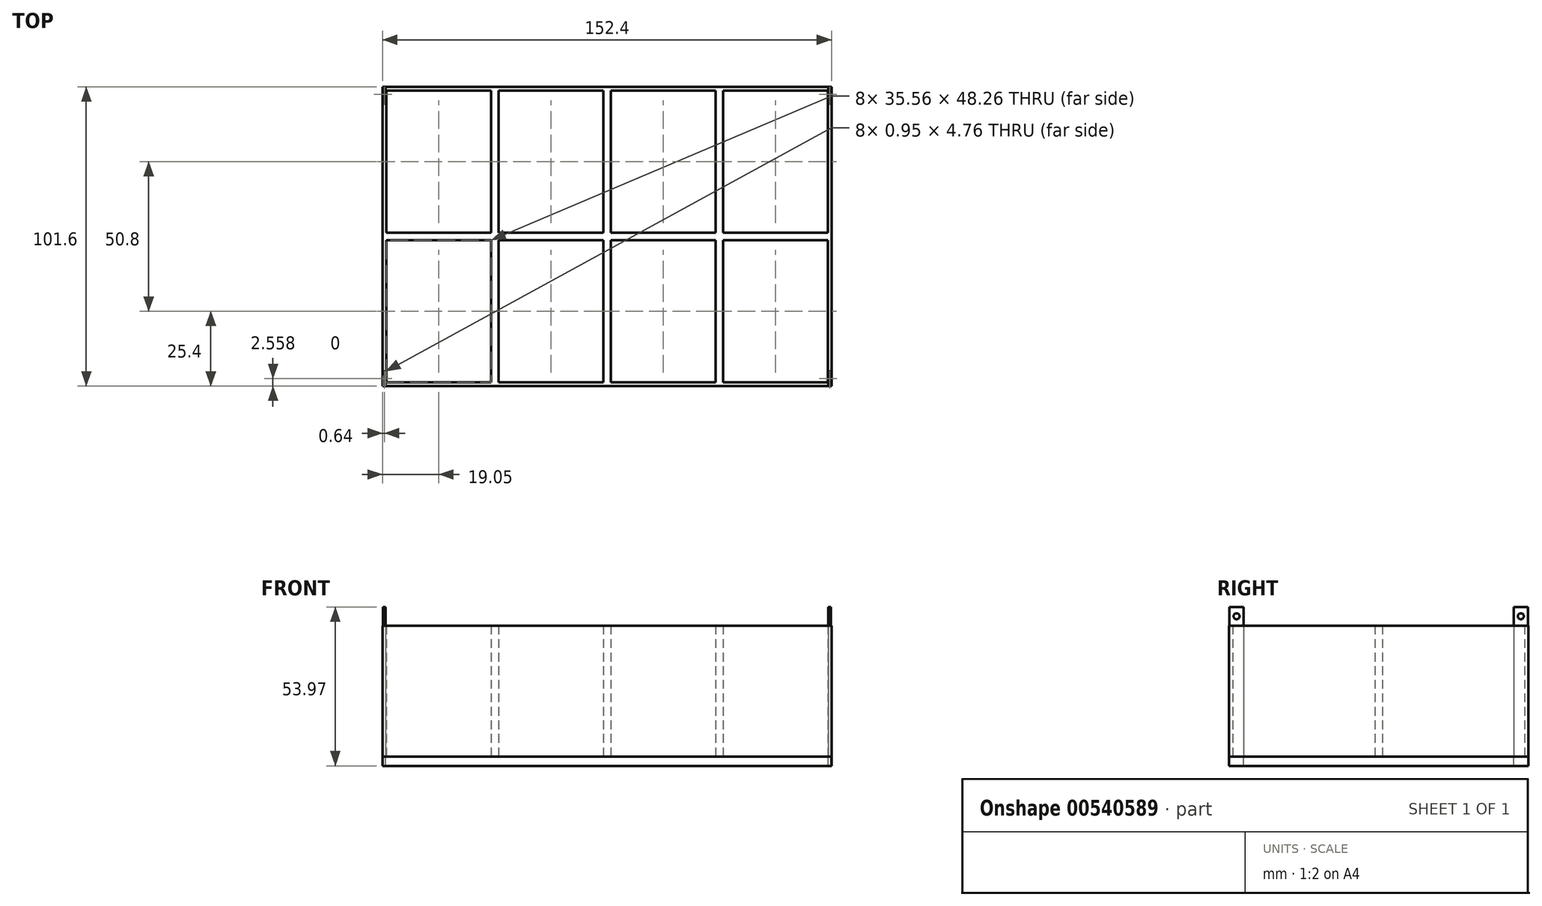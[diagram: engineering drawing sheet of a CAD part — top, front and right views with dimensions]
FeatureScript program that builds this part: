
annotation { "Feature Type Name" : "Feature", "Feature Type Description" : "" }
export const myFeature = defineFeature(function(context is Context, id is Id, definition is map)
    precondition{}
    {
        {
            var Q0;
            Q0=qCreatedBy(makeId("Top.planeOp"),FACE);
            var sketch = newSketch(context, id + "F0", { "sketchPlane" : qUnion([Q0])});
            skLineSegment(sketch, "E0.bottom", {"start": v(-76.2, 50.8) * mm, "end": v(76.2, 50.8) * mm});
            skLineSegment(sketch, "E0.top", {"start": v(-76.2, -50.8) * mm, "end": v(76.2, -50.8) * mm});
            skLineSegment(sketch, "E0.left", {"start": v(-76.2, 50.8) * mm, "end": v(-76.2, -50.8) * mm});
            skLineSegment(sketch, "E0.right", {"start": v(76.2, 50.8) * mm, "end": v(76.2, -50.8) * mm});
            skPoint(sketch, "E1", {"position": v(0, 0) * mm});
            skLineSegment(sketch, "E2.bottom", {"start": v(-74.93, 49.53) * mm, "end": v(-39.37, 49.53) * mm});
            skLineSegment(sketch, "E2.top", {"start": v(-74.93, 1.27) * mm, "end": v(-39.37, 1.27) * mm});
            skLineSegment(sketch, "E2.left", {"start": v(-74.93, 49.53) * mm, "end": v(-74.93, 1.27) * mm});
            skLineSegment(sketch, "E2.right", {"start": v(-39.37, 49.53) * mm, "end": v(-39.37, 1.27) * mm});
            skLineSegment(sketch, "E3.bottom", {"start": v(-36.83, 49.53) * mm, "end": v(-1.27, 49.53) * mm});
            skLineSegment(sketch, "E3.top", {"start": v(-36.83, 1.27) * mm, "end": v(-1.27, 1.27) * mm});
            skLineSegment(sketch, "E3.left", {"start": v(-36.83, 49.53) * mm, "end": v(-36.83, 1.27) * mm});
            skLineSegment(sketch, "E3.right", {"start": v(-1.27, 49.53) * mm, "end": v(-1.27, 1.27) * mm});
            skLineSegment(sketch, "E4.bottom", {"start": v(1.27, 49.53) * mm, "end": v(36.83, 49.53) * mm});
            skLineSegment(sketch, "E4.top", {"start": v(1.27, 1.27) * mm, "end": v(36.83, 1.27) * mm});
            skLineSegment(sketch, "E4.left", {"start": v(1.27, 49.53) * mm, "end": v(1.27, 1.27) * mm});
            skLineSegment(sketch, "E4.right", {"start": v(36.83, 49.53) * mm, "end": v(36.83, 1.27) * mm});
            skLineSegment(sketch, "E5.bottom", {"start": v(39.37, 49.53) * mm, "end": v(74.93, 49.53) * mm});
            skLineSegment(sketch, "E5.top", {"start": v(39.37, 1.27) * mm, "end": v(74.93, 1.27) * mm});
            skLineSegment(sketch, "E5.left", {"start": v(39.37, 49.53) * mm, "end": v(39.37, 1.27) * mm});
            skLineSegment(sketch, "E5.right", {"start": v(74.93, 49.53) * mm, "end": v(74.93, 1.27) * mm});
            skLineSegment(sketch, "E6", {"start": v(-38.1, 62.28) * mm, "end": v(-38.1, -57.18) * mm, "construction": true});
            skLineSegment(sketch, "E7", {"start": v(0, 55.51) * mm, "end": v(0, -66.66) * mm, "construction": true});
            skLineSegment(sketch, "E8", {"start": v(38.1, 55.29) * mm, "end": v(38.1, -59.88) * mm, "construction": true});
            skLineSegment(sketch, "E9", {"start": v(84.98, 0) * mm, "end": v(-105.69, 0) * mm, "construction": true});
            skLineSegment(sketch, "E10.MirrorCS", {"start": v(-39.37, -49.53) * mm, "end": v(-39.37, -1.27) * mm});
            skLineSegment(sketch, "E11.MirrorCS", {"start": v(-74.93, -49.53) * mm, "end": v(-39.37, -49.53) * mm});
            skLineSegment(sketch, "E12.MirrorCS", {"start": v(-74.93, -49.53) * mm, "end": v(-74.93, -1.27) * mm});
            skLineSegment(sketch, "E13.MirrorCS", {"start": v(-74.93, -1.27) * mm, "end": v(-39.37, -1.27) * mm});
            skLineSegment(sketch, "E14.MirrorCS", {"start": v(-36.83, -49.53) * mm, "end": v(-36.83, -1.27) * mm});
            skLineSegment(sketch, "E15.MirrorCS", {"start": v(-36.83, -49.53) * mm, "end": v(-1.27, -49.53) * mm});
            skLineSegment(sketch, "E16.MirrorCS", {"start": v(-1.27, -49.53) * mm, "end": v(-1.27, -1.27) * mm});
            skLineSegment(sketch, "E17.MirrorCS", {"start": v(1.27, -49.53) * mm, "end": v(1.27, -1.27) * mm});
            skLineSegment(sketch, "E18.MirrorCS", {"start": v(1.27, -49.53) * mm, "end": v(36.83, -49.53) * mm});
            skLineSegment(sketch, "E19.MirrorCS", {"start": v(36.83, -49.53) * mm, "end": v(36.83, -1.27) * mm});
            skLineSegment(sketch, "E20.MirrorCS", {"start": v(39.37, -49.53) * mm, "end": v(39.37, -1.27) * mm});
            skLineSegment(sketch, "E21.MirrorCS", {"start": v(39.37, -49.53) * mm, "end": v(74.93, -49.53) * mm});
            skLineSegment(sketch, "E22.MirrorCS", {"start": v(74.93, -49.53) * mm, "end": v(74.93, -1.27) * mm});
            skLineSegment(sketch, "E23.MirrorCS", {"start": v(39.37, -1.27) * mm, "end": v(74.93, -1.27) * mm});
            skLineSegment(sketch, "E24.MirrorCS", {"start": v(1.27, -1.27) * mm, "end": v(36.83, -1.27) * mm});
            skLineSegment(sketch, "E25.MirrorCS", {"start": v(-36.83, -1.27) * mm, "end": v(-1.27, -1.27) * mm});
            skLineSegment(sketch, "E26.bottom", {"start": v(-75.08, 45.86) * mm, "end": v(-76.04, 45.86) * mm});
            skLineSegment(sketch, "E26.top", {"start": v(-75.08, 50.62) * mm, "end": v(-76.04, 50.62) * mm});
            skLineSegment(sketch, "E26.left", {"start": v(-75.08, 45.86) * mm, "end": v(-75.08, 50.62) * mm});
            skLineSegment(sketch, "E26.right", {"start": v(-76.04, 45.86) * mm, "end": v(-76.04, 50.62) * mm});
            skPoint(sketch, "E26.middle", {"position": v(-75.56, 48.24) * mm});
            skLineSegment(sketch, "E27.MirrorCS", {"start": v(76.04, 45.86) * mm, "end": v(76.04, 50.62) * mm});
            skLineSegment(sketch, "E28.MirrorCS", {"start": v(75.08, 50.62) * mm, "end": v(76.04, 50.62) * mm});
            skLineSegment(sketch, "E29.MirrorCS", {"start": v(75.08, 45.86) * mm, "end": v(75.08, 50.62) * mm});
            skLineSegment(sketch, "E30.MirrorCS", {"start": v(75.08, 45.86) * mm, "end": v(76.04, 45.86) * mm});
            skLineSegment(sketch, "E31.MirrorCS", {"start": v(-76.04, -45.86) * mm, "end": v(-76.04, -50.62) * mm});
            skLineSegment(sketch, "E32.MirrorCS", {"start": v(-75.08, -50.62) * mm, "end": v(-76.04, -50.62) * mm});
            skLineSegment(sketch, "E33.MirrorCS", {"start": v(-75.08, -45.86) * mm, "end": v(-75.08, -50.62) * mm});
            skLineSegment(sketch, "E34.MirrorCS", {"start": v(-75.08, -45.86) * mm, "end": v(-76.04, -45.86) * mm});
            skLineSegment(sketch, "E35.MirrorCS", {"start": v(75.08, -45.86) * mm, "end": v(75.08, -50.62) * mm});
            skLineSegment(sketch, "E36.MirrorCS", {"start": v(75.08, -50.62) * mm, "end": v(76.04, -50.62) * mm});
            skLineSegment(sketch, "E37.MirrorCS", {"start": v(76.04, -45.86) * mm, "end": v(76.04, -50.62) * mm});
            skLineSegment(sketch, "E38.MirrorCS", {"start": v(75.08, -45.86) * mm, "end": v(76.04, -45.86) * mm});
            skSolve(sketch);
        }
        {
            var Q0;
            Q0=makeQuery(id+"F0.imprint","IMPRINT",FACE,{"disambiguationData":[TD([[makeQuery(id+"F0.imprint","IMPRINT",EDGE,{"derivedFrom":sQuery(id+"F0.wireOp",EDGE,"E0.bottom")}),-1.0]])]});
            var Q1;
            Q1=makeQuery(id+"F0.imprint","IMPRINT",FACE,{"disambiguationData":[TD([[makeQuery(id+"F0.imprint","IMPRINT",EDGE,{"derivedFrom":sQuery(id+"F0.wireOp",EDGE,"E2.bottom")}),-1.0]])]});
            var Q2;
            Q2=makeQuery(id+"F0.imprint","IMPRINT",FACE,{"disambiguationData":[TD([[makeQuery(id+"F0.imprint","IMPRINT",EDGE,{"derivedFrom":sQuery(id+"F0.wireOp",EDGE,"E3.bottom")}),-1.0]])]});
            var Q3;
            Q3=makeQuery(id+"F0.imprint","IMPRINT",FACE,{"disambiguationData":[TD([[makeQuery(id+"F0.imprint","IMPRINT",EDGE,{"derivedFrom":sQuery(id+"F0.wireOp",EDGE,"E4.bottom")}),-1.0]])]});
            var Q4;
            Q4=makeQuery(id+"F0.imprint","IMPRINT",FACE,{"disambiguationData":[TD([[makeQuery(id+"F0.imprint","IMPRINT",EDGE,{"derivedFrom":sQuery(id+"F0.wireOp",EDGE,"E5.bottom")}),-1.0]])]});
            var Q5;
            Q5=makeQuery(id+"F0.imprint","IMPRINT",FACE,{"disambiguationData":[TD([[makeQuery(id+"F0.imprint","IMPRINT",EDGE,{"derivedFrom":sQuery(id+"F0.wireOp",EDGE,"E20.MirrorCS")}),-1.0]])]});
            var Q6;
            Q6=makeQuery(id+"F0.imprint","IMPRINT",FACE,{"disambiguationData":[TD([[makeQuery(id+"F0.imprint","IMPRINT",EDGE,{"derivedFrom":sQuery(id+"F0.wireOp",EDGE,"E17.MirrorCS")}),-1.0]])]});
            var Q7;
            Q7=makeQuery(id+"F0.imprint","IMPRINT",FACE,{"disambiguationData":[TD([[makeQuery(id+"F0.imprint","IMPRINT",EDGE,{"derivedFrom":sQuery(id+"F0.wireOp",EDGE,"E14.MirrorCS")}),-1.0]])]});
            var Q8;
            Q8=makeQuery(id+"F0.imprint","IMPRINT",FACE,{"disambiguationData":[TD([[makeQuery(id+"F0.imprint","IMPRINT",EDGE,{"derivedFrom":sQuery(id+"F0.wireOp",EDGE,"E10.MirrorCS")}),1.0]])]});
            extrude(context, id + "F1", {"entities" : qUnion([Q0, Q1, Q2, Q3, Q4, Q5, Q6, Q7, Q8]), "oppositeDirection" : true, "depth" : 3.17 * mm, "offsetDistance" : 25.4 * mm});
        }
        {
            var Q0;
            Q0=makeQuery(id+"F0.imprint","IMPRINT",FACE,{"disambiguationData":[TD([[makeQuery(id+"F0.imprint","IMPRINT",EDGE,{"derivedFrom":sQuery(id+"F0.wireOp",EDGE,"E26.bottom")}),-1.0]])]});
            var Q1;
            Q1=makeQuery(id+"F0.imprint","IMPRINT",FACE,{"disambiguationData":[TD([[makeQuery(id+"F0.imprint","IMPRINT",EDGE,{"derivedFrom":sQuery(id+"F0.wireOp",EDGE,"E27.MirrorCS")}),1.0]])]});
            var Q2;
            Q2=makeQuery(id+"F0.imprint","IMPRINT",FACE,{"disambiguationData":[TD([[makeQuery(id+"F0.imprint","IMPRINT",EDGE,{"derivedFrom":sQuery(id+"F0.wireOp",EDGE,"E35.MirrorCS")}),1.0]])]});
            var Q3;
            Q3=makeQuery(id+"F0.imprint","IMPRINT",FACE,{"disambiguationData":[TD([[makeQuery(id+"F0.imprint","IMPRINT",EDGE,{"derivedFrom":sQuery(id+"F0.wireOp",EDGE,"E31.MirrorCS")}),1.0]])]});
            extrude(context, id + "F2", {"entities" : qUnion([Q0, Q1, Q2, Q3]), "depth" : 50.8 * mm, "offsetDistance" : 25.4 * mm});
        }
        {
            var Q0;
            Q0 = qSketchRegion(id + "F0", true);
            extrude(context, id + "F3", {"entities" : qUnion([Q0]), "depth" : 44.45 * mm, "offsetDistance" : 25.4 * mm});
        }
        {
            var Q0;
            Q0=makeQuery(id+"F2.opExtrude","SWEPT_FACE",FACE,{"disambiguationData":[OSD([sQuery(id+"F0.wireOp",EDGE,"E26.right")])]});
            var sketch = newSketch(context, id + "F4", { "sketchPlane" : qUnion([Q0])});
            skLineSegment(sketch, "E39", {"start": v(-48.24, 44.45) * mm, "end": v(-48.24, 50.8) * mm, "construction": true});
            skPoint(sketch, "E39.startSnap0", {"position": v(-48.24, 50.8) * mm});
            skPoint(sketch, "E40", {"position": v(-48.24, 47.63) * mm});
            skLineSegment(sketch, "E41", {"start": v(0, 70.84) * mm, "end": v(0, -51.58) * mm, "construction": true});
            skPoint(sketch, "E42.MirrorP", {"position": v(48.24, 47.63) * mm});
            skSolve(sketch);
        }
        {
            var Q0;
            Q0=sQuery(id+"F4.wireOp",VERTEX,"E40");
            var Q1;
            Q1=makeQuery(id+"F2.opExtrude","SWEPT_BODY",BODY,{"disambiguationData":[OSD([sQuery(id+"F0.wireOp",EDGE,"E26.bottom"),sQuery(id+"F0.wireOp",EDGE,"E26.top"),sQuery(id+"F0.wireOp",EDGE,"E26.left"),sQuery(id+"F0.wireOp",EDGE,"E26.right")])]});
            var Q2;
            Q2=makeQuery(id+"F2.opExtrude","SWEPT_BODY",BODY,{"disambiguationData":[OSD([sQuery(id+"F0.wireOp",EDGE,"E27.MirrorCS"),sQuery(id+"F0.wireOp",EDGE,"E28.MirrorCS"),sQuery(id+"F0.wireOp",EDGE,"E29.MirrorCS"),sQuery(id+"F0.wireOp",EDGE,"E30.MirrorCS")])]});
            hole(context, id + "F5", {"style" : HoleStyle.SIMPLE, "endStyle" : HoleEndStyle.THROUGH, "holeDiameter" : 2.03 * mm, "majorDiameter" : 6.35 * mm, "isTappedThrough" : true, "tappedDepth" : 12.7 * mm, "tapClearance" : 3, "locations" : qUnion([Q0]), "scope" : qUnion([Q1, Q2])});
        }
        {
            var Q0;
            Q0=sQuery(id+"F4.wireOp",VERTEX,"E42.MirrorP");
            var Q1;
            Q1=makeQuery(id+"F2.opExtrude","SWEPT_BODY",BODY,{"disambiguationData":[OSD([sQuery(id+"F0.wireOp",EDGE,"E31.MirrorCS"),sQuery(id+"F0.wireOp",EDGE,"E32.MirrorCS"),sQuery(id+"F0.wireOp",EDGE,"E33.MirrorCS"),sQuery(id+"F0.wireOp",EDGE,"E34.MirrorCS")])]});
            var Q2;
            Q2=makeQuery(id+"F2.opExtrude","SWEPT_BODY",BODY,{"disambiguationData":[OSD([sQuery(id+"F0.wireOp",EDGE,"E35.MirrorCS"),sQuery(id+"F0.wireOp",EDGE,"E36.MirrorCS"),sQuery(id+"F0.wireOp",EDGE,"E37.MirrorCS"),sQuery(id+"F0.wireOp",EDGE,"E38.MirrorCS")])]});
            hole(context, id + "F6", {"style" : HoleStyle.SIMPLE, "endStyle" : HoleEndStyle.THROUGH, "holeDiameter" : 2.03 * mm, "majorDiameter" : 6.35 * mm, "isTappedThrough" : true, "tappedDepth" : 12.7 * mm, "tapClearance" : 3, "locations" : qUnion([Q0]), "scope" : qUnion([Q1, Q2])});
        }
    });
